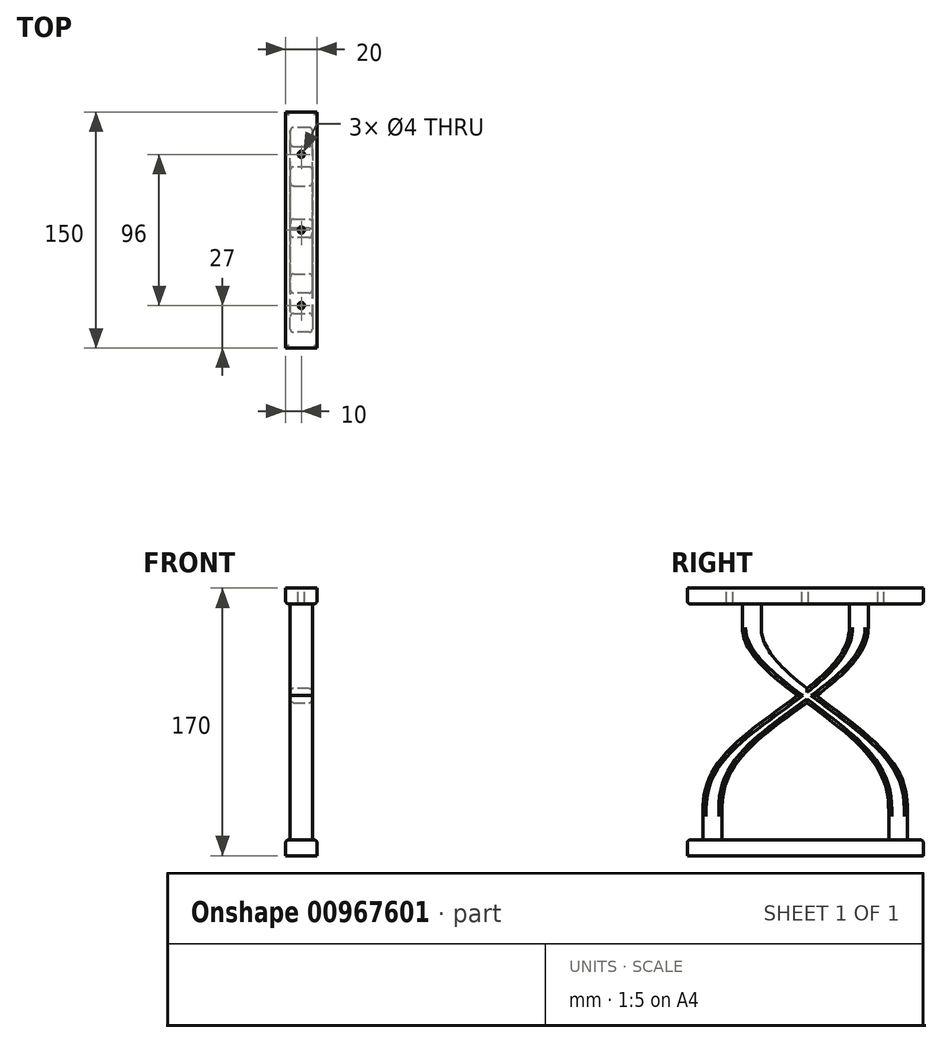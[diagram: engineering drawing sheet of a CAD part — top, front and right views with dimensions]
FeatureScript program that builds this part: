
annotation { "Feature Type Name" : "Feature", "Feature Type Description" : "" }
export const myFeature = defineFeature(function(context is Context, id is Id, definition is map)
    precondition{}
    {
        {
            var Q0;
            Q0=qCreatedBy(makeId("Right.planeOp"),FACE);
            var sketch = newSketch(context, id + "F0", { "sketchPlane" : qUnion([Q0])});
            skLineSegment(sketch, "E0", {"start": v(-75, 0) * mm, "end": v(75, 0) * mm});
            skLineSegment(sketch, "E1", {"start": v(-75, 0) * mm, "end": v(-75, -10) * mm});
            skLineSegment(sketch, "E2", {"start": v(-75, -10) * mm, "end": v(75, -10) * mm});
            skLineSegment(sketch, "E3", {"start": v(75, -10) * mm, "end": v(75, 0) * mm});
            skLineSegment(sketch, "E4", {"start": v(-75, 160) * mm, "end": v(75, 160) * mm});
            skLineSegment(sketch, "E5", {"start": v(75, 160) * mm, "end": v(75, 150) * mm});
            skLineSegment(sketch, "E6", {"start": v(75, 150) * mm, "end": v(-75, 150) * mm});
            skLineSegment(sketch, "E7", {"start": v(-75, 150) * mm, "end": v(-75, 160) * mm});
            skSolve(sketch);
        }
        {
            var Q0;
            Q0 = qSketchRegion(id + "F0", true);
            extrude(context, id + "F1", {"entities" : qUnion([Q0]), "depth" : 20 * mm, "offsetDistance" : 25 * mm});
        }
        {
            var Q0;
            Q0=makeQuery(id+"F1.opExtrude","SWEPT_FACE",FACE,{"disambiguationData":[OSD([sQuery(id+"F0.wireOp",EDGE,"E0")])]});
            var sketch = newSketch(context, id + "F2", { "sketchPlane" : qUnion([Q0])});
            skLineSegment(sketch, "E8.top", {"start": v(2.5, -75) * mm, "end": v(17.5, -75) * mm});
            skLineSegment(sketch, "E9", {"start": v(35.37, 0) * mm, "end": v(-77.59, 0) * mm, "construction": true});
            skLineSegment(sketch, "E10", {"start": v(10, -75) * mm, "end": v(10, 75) * mm, "construction": true});
            skLineSegment(sketch, "E11", {"start": v(17, -65) * mm, "end": v(3, -65) * mm});
            skLineSegment(sketch, "E12", {"start": v(3, -65) * mm, "end": v(3, -53) * mm});
            skLineSegment(sketch, "E13", {"start": v(3, -53) * mm, "end": v(17, -53) * mm});
            skLineSegment(sketch, "E14", {"start": v(17, -53) * mm, "end": v(17, -65) * mm});
            skLineSegment(sketch, "E15.MirrorCS", {"start": v(3, 53) * mm, "end": v(17, 53) * mm});
            skLineSegment(sketch, "E16.MirrorCS", {"start": v(17, 53) * mm, "end": v(17, 65) * mm});
            skLineSegment(sketch, "E17.MirrorCS", {"start": v(3, 65) * mm, "end": v(3, 53) * mm});
            skLineSegment(sketch, "E18.MirrorCS", {"start": v(17, 65) * mm, "end": v(3, 65) * mm});
            skSolve(sketch);
        }
        {
            var Q0;
            Q0=makeQuery(id+"F1.opExtrude","SWEPT_FACE",FACE,{"disambiguationData":[OSD([sQuery(id+"F0.wireOp",EDGE,"E6")])]});
            var sketch = newSketch(context, id + "F3", { "sketchPlane" : qUnion([Q0])});
            skLineSegment(sketch, "E19.top", {"start": v(2.67, -50) * mm, "end": v(17.33, -50) * mm});
            skLineSegment(sketch, "E20", {"start": v(35.54, 0) * mm, "end": v(-77.42, 0) * mm, "construction": true});
            skLineSegment(sketch, "E21", {"start": v(10, -50) * mm, "end": v(10, 200) * mm, "construction": true});
            skLineSegment(sketch, "E22", {"start": v(17, -40) * mm, "end": v(3, -40) * mm});
            skLineSegment(sketch, "E23", {"start": v(3, -40) * mm, "end": v(3, -28) * mm});
            skLineSegment(sketch, "E24", {"start": v(3, -28) * mm, "end": v(17, -28) * mm});
            skLineSegment(sketch, "E25", {"start": v(17, -28) * mm, "end": v(17, -40) * mm});
            skLineSegment(sketch, "E26.MirrorCS", {"start": v(3, 28) * mm, "end": v(17, 28) * mm});
            skLineSegment(sketch, "E27.MirrorCS", {"start": v(17, 28) * mm, "end": v(17, 40) * mm});
            skLineSegment(sketch, "E28.MirrorCS", {"start": v(3, 40) * mm, "end": v(3, 28) * mm});
            skLineSegment(sketch, "E29.MirrorCS", {"start": v(17, 40) * mm, "end": v(3, 40) * mm});
            skSolve(sketch);
        }
        {
            var Q0;
            Q0 = qSketchRegion(id + "F2", true);
            extrude(context, id + "F4", {"entities" : qUnion([Q0]), "operationType" : NewBodyOperationType.ADD, "depth" : 15 * mm, "offsetDistance" : 25 * mm});
        }
        {
            var Q0;
            Q0 = qSketchRegion(id + "F3", true);
            extrude(context, id + "F5", {"entities" : qUnion([Q0]), "operationType" : NewBodyOperationType.ADD, "depth" : 15 * mm, "offsetDistance" : 25 * mm});
        }
        {
            var Q0;
            Q0=makeQuery(id+"F5.opExtrude","CAP_FACE",FACE,{"disambiguationData":[OSD([sQuery(id+"F3.wireOp",EDGE,"E26.MirrorCS"),sQuery(id+"F3.wireOp",EDGE,"E27.MirrorCS"),sQuery(id+"F3.wireOp",EDGE,"E28.MirrorCS"),sQuery(id+"F3.wireOp",EDGE,"E29.MirrorCS")])],"isStart":false});
            var Q1;
            Q1=makeQuery(id+"F4.opExtrude","CAP_FACE",FACE,{"disambiguationData":[OSD([sQuery(id+"F2.wireOp",EDGE,"E15.MirrorCS"),sQuery(id+"F2.wireOp",EDGE,"E16.MirrorCS"),sQuery(id+"F2.wireOp",EDGE,"E17.MirrorCS"),sQuery(id+"F2.wireOp",EDGE,"E18.MirrorCS")])],"isStart":false});
            loft(context, id + "F6", {"startCondition" : LoftEndDerivativeType.MATCH_TANGENT, "startMagnitude" : 0.9, "endCondition" : LoftEndDerivativeType.MATCH_CURVATURE, "endMagnitude" : 1, "sheetProfilesArray" : [{ "sheetProfileEntities" : qUnion([Q0]) }, { "sheetProfileEntities" : qUnion([Q1]) }]});
        }
        {
            var Q0;
            Q0=makeQuery(id+"F5.opExtrude","CAP_FACE",FACE,{"disambiguationData":[OSD([sQuery(id+"F3.wireOp",EDGE,"E22"),sQuery(id+"F3.wireOp",EDGE,"E23"),sQuery(id+"F3.wireOp",EDGE,"E24"),sQuery(id+"F3.wireOp",EDGE,"E25")])],"isStart":false});
            var Q1;
            Q1=makeQuery(id+"F4.opExtrude","CAP_FACE",FACE,{"disambiguationData":[OSD([sQuery(id+"F2.wireOp",EDGE,"E11"),sQuery(id+"F2.wireOp",EDGE,"E12"),sQuery(id+"F2.wireOp",EDGE,"E13"),sQuery(id+"F2.wireOp",EDGE,"E14")])],"isStart":false});
            loft(context, id + "F7", {"startCondition" : LoftEndDerivativeType.MATCH_TANGENT, "startMagnitude" : 1, "endCondition" : LoftEndDerivativeType.MATCH_CURVATURE, "endMagnitude" : 1, "sheetProfilesArray" : [{ "sheetProfileEntities" : qUnion([Q0]) }, { "sheetProfileEntities" : qUnion([Q1]) }]});
        }
        {
            var Q0;
            Q0=makeQuery(id+"F1.opExtrude","SWEPT_FACE",FACE,{"disambiguationData":[OSD([sQuery(id+"F0.wireOp",EDGE,"E4")])]});
            var sketch = newSketch(context, id + "F8", { "sketchPlane" : qUnion([Q0])});
            skCircle(sketch, "E30", {"center": v(10, -48) * mm, "radius": 2 * mm});
            skPoint(sketch, "E30.centerSnap0", {"position": v(10, -75) * mm});
            skCircle(sketch, "E31", {"center": v(10, 0) * mm, "radius": 2 * mm});
            skPoint(sketch, "E31.centerSnap0", {"position": v(10, 75) * mm});
            skLineSegment(sketch, "E32", {"start": v(-1.78, 0) * mm, "end": v(16.32, 0) * mm, "construction": true});
            skCircle(sketch, "E33.MirrorC", {"center": v(10, 48) * mm, "radius": 2 * mm});
            skSolve(sketch);
        }
        {
            var Q0;
            Q0 = qSketchRegion(id + "F8", true);
            extrude(context, id + "F9", {"entities" : qUnion([Q0]), "operationType" : NewBodyOperationType.REMOVE, "endBound" : BoundingType.UP_TO_NEXT, "oppositeDirection" : true, "depth" : 25 * mm, "offsetDistance" : 25 * mm});
        }
        {
            var Q0;
            Q0=makeQuery(id+"F1.opExtrude","SWEPT_BODY",BODY,{"disambiguationData":[OSD([sQuery(id+"F0.wireOp",EDGE,"E4"),sQuery(id+"F0.wireOp",EDGE,"E5"),sQuery(id+"F0.wireOp",EDGE,"E6"),sQuery(id+"F0.wireOp",EDGE,"E7")])]});
            var Q1;
            Q1=makeQuery(id+"F6.opLoft","SWEPT_BODY",BODY,{"disambiguationData":[OSD([sQuery(id+"F2.wireOp",EDGE,"E15.MirrorCS"),sQuery(id+"F2.wireOp",EDGE,"E16.MirrorCS"),sQuery(id+"F2.wireOp",EDGE,"E17.MirrorCS"),sQuery(id+"F2.wireOp",EDGE,"E18.MirrorCS"),sQuery(id+"F3.wireOp",EDGE,"E26.MirrorCS"),sQuery(id+"F3.wireOp",EDGE,"E27.MirrorCS"),sQuery(id+"F3.wireOp",EDGE,"E28.MirrorCS"),sQuery(id+"F3.wireOp",EDGE,"E29.MirrorCS")])]});
            var Q2;
            Q2=makeQuery(id+"F7.opLoft","SWEPT_BODY",BODY,{"disambiguationData":[OSD([sQuery(id+"F2.wireOp",EDGE,"E11"),sQuery(id+"F2.wireOp",EDGE,"E12"),sQuery(id+"F2.wireOp",EDGE,"E13"),sQuery(id+"F2.wireOp",EDGE,"E14"),sQuery(id+"F3.wireOp",EDGE,"E22"),sQuery(id+"F3.wireOp",EDGE,"E23"),sQuery(id+"F3.wireOp",EDGE,"E24"),sQuery(id+"F3.wireOp",EDGE,"E25")])]});
            var Q3;
            Q3=makeQuery(id+"F1.opExtrude","SWEPT_BODY",BODY,{"disambiguationData":[OSD([sQuery(id+"F0.wireOp",EDGE,"E0"),sQuery(id+"F0.wireOp",EDGE,"E1"),sQuery(id+"F0.wireOp",EDGE,"E2"),sQuery(id+"F0.wireOp",EDGE,"E3")])]});
            booleanBodies(context, id + "F10", {"operationType" : BooleanOperationType.UNION, "tools" : qUnion([Q0, Q1, Q2, Q3])});
        }
        {
            var Q0;
            {var subQ4=sQuery(id+"F2.wireOp",EDGE,"E17.MirrorCS");var subQ5=sQuery(id+"F3.wireOp",EDGE,"E26.MirrorCS");var subQ6=sQuery(id+"F3.wireOp",EDGE,"E28.MirrorCS");var subQ7=sQuery(id+"F2.wireOp",EDGE,"E18.MirrorCS");Q0=makeQuery(id+"F10.opBoolean","SPLIT",EDGE,{"disambiguationData":[TD([makeQuery(id+"F5.opExtrude","SWEPT_FACE",FACE,{"disambiguationData":[OSD([subQ5])]})])],"derivedFrom":makeQuery(id+"F6.opLoft","SWEPT_EDGE",EDGE,{"disambiguationData":[OSD([subQ4,subQ7,subQ5,subQ6])]})});}
            var Q1;
            {var subQ0=sQuery(id+"F3.wireOp",EDGE,"E24");var subQ1=sQuery(id+"F3.wireOp",EDGE,"E23");var subQ2=sQuery(id+"F2.wireOp",EDGE,"E12");var subQ3=sQuery(id+"F2.wireOp",EDGE,"E11");Q1=makeQuery(id+"F10.opBoolean","SPLIT",EDGE,{"disambiguationData":[TD([makeQuery(id+"F5.opExtrude","SWEPT_FACE",FACE,{"disambiguationData":[OSD([subQ0])]})])],"derivedFrom":makeQuery(id+"F7.opLoft","SWEPT_EDGE",EDGE,{"disambiguationData":[OSD([subQ3,subQ2,subQ1,subQ0])]})});}
            var Q2;
            {var subQ0=sQuery(id+"F3.wireOp",EDGE,"E25");var subQ1=sQuery(id+"F3.wireOp",EDGE,"E24");var subQ3=sQuery(id+"F2.wireOp",EDGE,"E14");var subQ4=sQuery(id+"F2.wireOp",EDGE,"E11");Q2=makeQuery(id+"F10.opBoolean","SPLIT",EDGE,{"disambiguationData":[TD([makeQuery(id+"F5.opExtrude","SWEPT_FACE",FACE,{"disambiguationData":[OSD([subQ1])]})])],"derivedFrom":makeQuery(id+"F7.opLoft","SWEPT_EDGE",EDGE,{"disambiguationData":[OSD([subQ4,subQ3,subQ1,subQ0])]})});}
            var Q3;
            {var subQ0=sQuery(id+"F3.wireOp",EDGE,"E25");var subQ1=sQuery(id+"F3.wireOp",EDGE,"E22");var subQ6=sQuery(id+"F2.wireOp",EDGE,"E14");var subQ7=sQuery(id+"F2.wireOp",EDGE,"E13");Q3=makeQuery(id+"F10.opBoolean","SPLIT",EDGE,{"disambiguationData":[TD([makeQuery(id+"F5.opExtrude","SWEPT_FACE",FACE,{"disambiguationData":[OSD([subQ1])]})])],"derivedFrom":makeQuery(id+"F7.opLoft","SWEPT_EDGE",EDGE,{"disambiguationData":[OSD([subQ7,subQ6,subQ1,subQ0])]})});}
            var Q4;
            {var subQ0=sQuery(id+"F3.wireOp",EDGE,"E22");var subQ5=sQuery(id+"F3.wireOp",EDGE,"E23");var subQ6=sQuery(id+"F2.wireOp",EDGE,"E13");var subQ7=sQuery(id+"F2.wireOp",EDGE,"E12");Q4=makeQuery(id+"F10.opBoolean","SPLIT",EDGE,{"disambiguationData":[TD([makeQuery(id+"F5.opExtrude","SWEPT_FACE",FACE,{"disambiguationData":[OSD([subQ0])]})])],"derivedFrom":makeQuery(id+"F7.opLoft","SWEPT_EDGE",EDGE,{"disambiguationData":[OSD([subQ7,subQ6,subQ0,subQ5])]})});}
            var Q5;
            {var subQ0=sQuery(id+"F3.wireOp",EDGE,"E25");var subQ2=sQuery(id+"F3.wireOp",EDGE,"E24");var subQ3=sQuery(id+"F2.wireOp",EDGE,"E14");var subQ4=sQuery(id+"F2.wireOp",EDGE,"E11");Q5=makeQuery(id+"F10.opBoolean","SPLIT",EDGE,{"disambiguationData":[TD([makeQuery(id+"F4.opExtrude","SWEPT_FACE",FACE,{"disambiguationData":[OSD([subQ4])]})])],"derivedFrom":makeQuery(id+"F7.opLoft","SWEPT_EDGE",EDGE,{"disambiguationData":[OSD([subQ4,subQ3,subQ2,subQ0])]})});}
            var Q6;
            {var subQ0=sQuery(id+"F2.wireOp",EDGE,"E12");var subQ1=sQuery(id+"F3.wireOp",EDGE,"E23");var subQ2=sQuery(id+"F2.wireOp",EDGE,"E11");var subQ3=sQuery(id+"F3.wireOp",EDGE,"E24");Q6=makeQuery(id+"F10.opBoolean","SPLIT",EDGE,{"disambiguationData":[TD([makeQuery(id+"F4.opExtrude","SWEPT_FACE",FACE,{"disambiguationData":[OSD([subQ2])]})])],"derivedFrom":makeQuery(id+"F7.opLoft","SWEPT_EDGE",EDGE,{"disambiguationData":[OSD([subQ2,subQ0,subQ1,subQ3])]})});}
            var Q7;
            {var subQ0=sQuery(id+"F3.wireOp",EDGE,"E23");var subQ1=sQuery(id+"F3.wireOp",EDGE,"E22");var subQ2=sQuery(id+"F2.wireOp",EDGE,"E13");var subQ3=sQuery(id+"F2.wireOp",EDGE,"E12");Q7=makeQuery(id+"F10.opBoolean","SPLIT",EDGE,{"disambiguationData":[TD([makeQuery(id+"F4.opExtrude","SWEPT_FACE",FACE,{"disambiguationData":[OSD([subQ2])]})])],"derivedFrom":makeQuery(id+"F7.opLoft","SWEPT_EDGE",EDGE,{"disambiguationData":[OSD([subQ3,subQ2,subQ1,subQ0])]})});}
            var Q8;
            {var subQ4=sQuery(id+"F2.wireOp",EDGE,"E17.MirrorCS");var subQ5=sQuery(id+"F2.wireOp",EDGE,"E15.MirrorCS");var subQ6=sQuery(id+"F3.wireOp",EDGE,"E29.MirrorCS");var subQ7=sQuery(id+"F3.wireOp",EDGE,"E28.MirrorCS");Q8=makeQuery(id+"F10.opBoolean","SPLIT",EDGE,{"disambiguationData":[TD([makeQuery(id+"F4.opExtrude","SWEPT_FACE",FACE,{"disambiguationData":[OSD([subQ5])]})])],"derivedFrom":makeQuery(id+"F6.opLoft","SWEPT_EDGE",EDGE,{"disambiguationData":[OSD([subQ5,subQ4,subQ7,subQ6])]})});}
            var Q9;
            {var subQ0=sQuery(id+"F2.wireOp",EDGE,"E18.MirrorCS");var subQ5=sQuery(id+"F2.wireOp",EDGE,"E17.MirrorCS");var subQ6=sQuery(id+"F3.wireOp",EDGE,"E28.MirrorCS");var subQ7=sQuery(id+"F3.wireOp",EDGE,"E26.MirrorCS");Q9=makeQuery(id+"F10.opBoolean","SPLIT",EDGE,{"disambiguationData":[TD([makeQuery(id+"F4.opExtrude","SWEPT_FACE",FACE,{"disambiguationData":[OSD([subQ0])]})])],"derivedFrom":makeQuery(id+"F6.opLoft","SWEPT_EDGE",EDGE,{"disambiguationData":[OSD([subQ5,subQ0,subQ7,subQ6])]})});}
            var Q10;
            {var subQ1=sQuery(id+"F2.wireOp",EDGE,"E18.MirrorCS");var subQ2=sQuery(id+"F2.wireOp",EDGE,"E16.MirrorCS");var subQ4=sQuery(id+"F3.wireOp",EDGE,"E27.MirrorCS");var subQ5=sQuery(id+"F3.wireOp",EDGE,"E26.MirrorCS");Q10=makeQuery(id+"F10.opBoolean","SPLIT",EDGE,{"disambiguationData":[TD([makeQuery(id+"F4.opExtrude","SWEPT_FACE",FACE,{"disambiguationData":[OSD([subQ1])]})])],"derivedFrom":makeQuery(id+"F6.opLoft","SWEPT_EDGE",EDGE,{"disambiguationData":[OSD([subQ2,subQ1,subQ5,subQ4])]})});}
            var Q11;
            {var subQ1=sQuery(id+"F2.wireOp",EDGE,"E16.MirrorCS");var subQ2=sQuery(id+"F2.wireOp",EDGE,"E15.MirrorCS");var subQ3=sQuery(id+"F3.wireOp",EDGE,"E27.MirrorCS");var subQ5=sQuery(id+"F3.wireOp",EDGE,"E29.MirrorCS");Q11=makeQuery(id+"F10.opBoolean","SPLIT",EDGE,{"disambiguationData":[TD([makeQuery(id+"F4.opExtrude","SWEPT_FACE",FACE,{"disambiguationData":[OSD([subQ2])]})])],"derivedFrom":makeQuery(id+"F6.opLoft","SWEPT_EDGE",EDGE,{"disambiguationData":[OSD([subQ2,subQ1,subQ3,subQ5])]})});}
            var Q12;
            {var subQ0=sQuery(id+"F3.wireOp",EDGE,"E25");var subQ1=sQuery(id+"F2.wireOp",EDGE,"E14");var subQ6=sQuery(id+"F2.wireOp",EDGE,"E13");var subQ7=sQuery(id+"F3.wireOp",EDGE,"E22");Q12=makeQuery(id+"F10.opBoolean","SPLIT",EDGE,{"disambiguationData":[TD([makeQuery(id+"F4.opExtrude","SWEPT_FACE",FACE,{"disambiguationData":[OSD([subQ6])]})])],"derivedFrom":makeQuery(id+"F7.opLoft","SWEPT_EDGE",EDGE,{"disambiguationData":[OSD([subQ6,subQ1,subQ7,subQ0])]})});}
            var Q13;
            {var subQ0=sQuery(id+"F3.wireOp",EDGE,"E26.MirrorCS");var subQ2=sQuery(id+"F2.wireOp",EDGE,"E16.MirrorCS");var subQ6=sQuery(id+"F3.wireOp",EDGE,"E27.MirrorCS");var subQ7=sQuery(id+"F2.wireOp",EDGE,"E18.MirrorCS");Q13=makeQuery(id+"F10.opBoolean","SPLIT",EDGE,{"disambiguationData":[TD([makeQuery(id+"F5.opExtrude","SWEPT_FACE",FACE,{"disambiguationData":[OSD([subQ0])]})])],"derivedFrom":makeQuery(id+"F6.opLoft","SWEPT_EDGE",EDGE,{"disambiguationData":[OSD([subQ2,subQ7,subQ0,subQ6])]})});}
            var Q14;
            {var subQ0=sQuery(id+"F3.wireOp",EDGE,"E27.MirrorCS");var subQ2=sQuery(id+"F2.wireOp",EDGE,"E16.MirrorCS");var subQ6=sQuery(id+"F3.wireOp",EDGE,"E29.MirrorCS");var subQ7=sQuery(id+"F2.wireOp",EDGE,"E15.MirrorCS");Q14=makeQuery(id+"F10.opBoolean","SPLIT",EDGE,{"disambiguationData":[TD([makeQuery(id+"F5.opExtrude","SWEPT_FACE",FACE,{"disambiguationData":[OSD([subQ6])]})])],"derivedFrom":makeQuery(id+"F6.opLoft","SWEPT_EDGE",EDGE,{"disambiguationData":[OSD([subQ7,subQ2,subQ0,subQ6])]})});}
            var Q15;
            {var subQ0=sQuery(id+"F3.wireOp",EDGE,"E28.MirrorCS");var subQ5=sQuery(id+"F2.wireOp",EDGE,"E17.MirrorCS");var subQ6=sQuery(id+"F3.wireOp",EDGE,"E29.MirrorCS");var subQ7=sQuery(id+"F2.wireOp",EDGE,"E15.MirrorCS");Q15=makeQuery(id+"F10.opBoolean","SPLIT",EDGE,{"disambiguationData":[TD([makeQuery(id+"F5.opExtrude","SWEPT_FACE",FACE,{"disambiguationData":[OSD([subQ6])]})])],"derivedFrom":makeQuery(id+"F6.opLoft","SWEPT_EDGE",EDGE,{"disambiguationData":[OSD([subQ7,subQ5,subQ0,subQ6])]})});}
            fillet(context, id + "F11", {"entities" : qUnion([Q0, Q1, Q2, Q3, Q4, Q5, Q6, Q7, Q8, Q9, Q10, Q11, Q12, Q13, Q14, Q15]), "radius" : 2 * mm, "tangentPropagation" : true, "allowEdgeOverflow" : false});
        }
        {
            var Q0;
            Q0=makeQuery(id+"F1.opExtrude","SWEPT_EDGE",EDGE,{"disambiguationData":[OSD([sQuery(id+"F0.wireOp",EDGE,"E6"),sQuery(id+"F0.wireOp",EDGE,"E7")])]});
            var Q1;
            Q1=makeQuery(id+"F1.opExtrude","SWEPT_EDGE",EDGE,{"disambiguationData":[OSD([sQuery(id+"F0.wireOp",EDGE,"E5"),sQuery(id+"F0.wireOp",EDGE,"E6")])]});
            var Q2;
            Q2=makeQuery(id+"F1.opExtrude","CAP_EDGE",EDGE,{"disambiguationData":[OSD([sQuery(id+"F0.wireOp",EDGE,"E6")])],"isStart":false});
            var Q3;
            Q3=makeQuery(id+"F1.opExtrude","CAP_EDGE",EDGE,{"disambiguationData":[OSD([sQuery(id+"F0.wireOp",EDGE,"E6")])],"isStart":true});
            var Q4;
            Q4=makeQuery(id+"F1.opExtrude","CAP_EDGE",EDGE,{"disambiguationData":[OSD([sQuery(id+"F0.wireOp",EDGE,"E0")])],"isStart":false});
            var Q5;
            Q5=makeQuery(id+"F1.opExtrude","CAP_EDGE",EDGE,{"disambiguationData":[OSD([sQuery(id+"F0.wireOp",EDGE,"E0")])],"isStart":true});
            var Q6;
            Q6=makeQuery(id+"F1.opExtrude","SWEPT_EDGE",EDGE,{"disambiguationData":[OSD([sQuery(id+"F0.wireOp",EDGE,"E0"),sQuery(id+"F0.wireOp",EDGE,"E3")])]});
            var Q7;
            Q7=makeQuery(id+"F1.opExtrude","SWEPT_EDGE",EDGE,{"disambiguationData":[OSD([sQuery(id+"F0.wireOp",EDGE,"E0"),sQuery(id+"F0.wireOp",EDGE,"E1")])]});
            var Q8;
            Q8=makeQuery(id+"F1.opExtrude","CAP_EDGE",EDGE,{"disambiguationData":[OSD([sQuery(id+"F0.wireOp",EDGE,"E1")])],"isStart":false});
            var Q9;
            Q9=makeQuery(id+"F1.opExtrude","CAP_EDGE",EDGE,{"disambiguationData":[OSD([sQuery(id+"F0.wireOp",EDGE,"E1")])],"isStart":true});
            var Q10;
            Q10=makeQuery(id+"F1.opExtrude","CAP_EDGE",EDGE,{"disambiguationData":[OSD([sQuery(id+"F0.wireOp",EDGE,"E3")])],"isStart":true});
            var Q11;
            Q11=makeQuery(id+"F1.opExtrude","CAP_EDGE",EDGE,{"disambiguationData":[OSD([sQuery(id+"F0.wireOp",EDGE,"E3")])],"isStart":false});
            fillet(context, id + "F12", {"entities" : qUnion([Q0, Q1, Q2, Q3, Q4, Q5, Q6, Q7, Q8, Q9, Q10, Q11]), "radius" : 2 * mm, "tangentPropagation" : true, "allowEdgeOverflow" : false});
        }
    });
